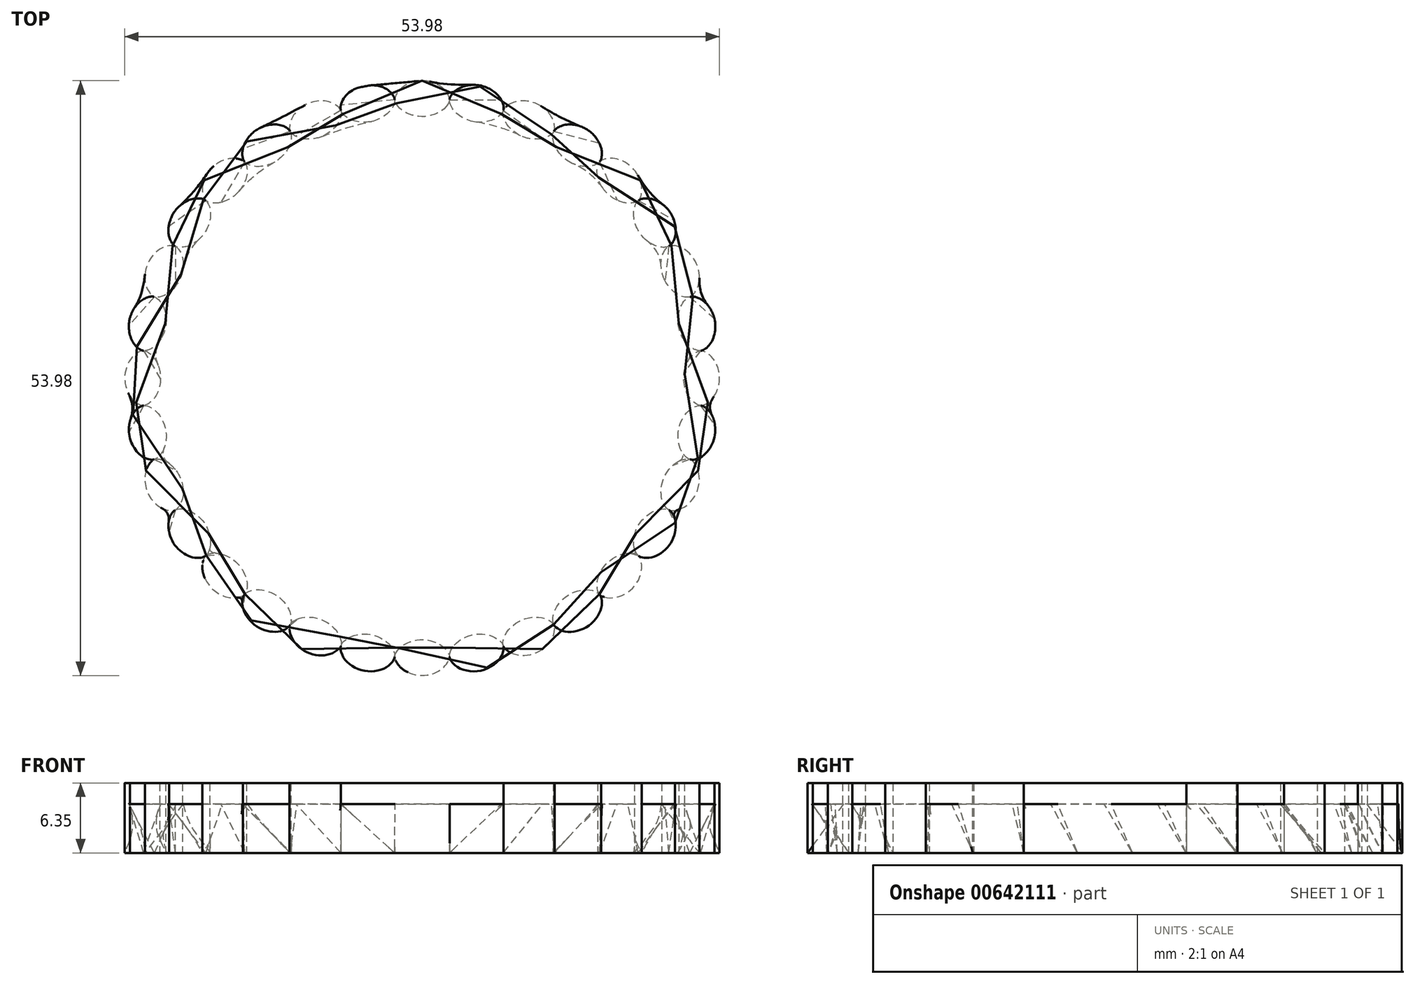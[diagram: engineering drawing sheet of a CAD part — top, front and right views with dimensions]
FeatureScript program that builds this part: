
annotation { "Feature Type Name" : "Feature", "Feature Type Description" : "" }
export const myFeature = defineFeature(function(context is Context, id is Id, definition is map)
    precondition{}
    {
        {
            var Q0;
            Q0=qCreatedBy(makeId("Top.planeOp"),FACE);
            var sketch = newSketch(context, id + "F0", { "sketchPlane" : qUnion([Q0])});
            skCircle(sketch, "E0", {"center": v(0, 0) * mm, "radius": 25.4 * mm, "construction": true});
            skCircle(sketch, "E1", {"center": v(0, 26.2) * mm, "radius": 0.8 * mm, "construction": true});
            skLineSegment(sketch, "E2", {"start": v(0, 26.99) * mm, "end": v(0, 26.2) * mm, "construction": true});
            skLineSegment(sketch, "E3", {"start": v(0, 0) * mm, "end": v(-4.8, 24.13) * mm, "construction": true});
            skCircle(sketch, "E4", {"center": v(-4.8, 24.13) * mm, "radius": 0.8 * mm, "construction": true});
            skLineSegment(sketch, "E5", {"start": v(0, 0) * mm, "end": v(0, 26.99) * mm, "construction": true});
            skCircle(sketch, "E6", {"center": v(0, 0) * mm, "radius": 26.99 * mm, "construction": true});
            skLineSegment(sketch, "E7", {"start": v(0, 0) * mm, "end": v(-2.49, 25.28) * mm, "construction": true});
            skLineSegment(sketch, "E8", {"start": v(0, 0) * mm, "end": v(-10.33, 24.93) * mm, "construction": true});
            skLineSegment(sketch, "E9", {"start": v(0, 0) * mm, "end": v(-7.37, 24.3) * mm, "construction": true});
            skCircle(sketch, "E10", {"center": v(-10.02, 24.2) * mm, "radius": 0.8 * mm, "construction": true});
            skCircle(sketch, "E11", {"center": v(-1.29, 26.16) * mm, "radius": 0.8 * mm, "construction": true});
            skCircle(sketch, "E12", {"center": v(-3.61, 24.34) * mm, "radius": 0.8 * mm, "construction": true});
            skLineSegment(sketch, "E13", {"start": v(-1.29, 26.16) * mm, "end": v(0, 0) * mm, "construction": true});
            skLineSegment(sketch, "E14", {"start": v(0, 0) * mm, "end": v(-3.61, 24.34) * mm, "construction": true});
            skLineSegment(sketch, "E15", {"start": v(-3.61, 24.34) * mm, "end": v(-2.83, 24.46) * mm, "construction": true});
            skLineSegment(sketch, "E16", {"start": v(-1.29, 26.16) * mm, "end": v(-2.08, 26.12) * mm, "construction": true});
            skPoint(sketch, "E17", {"position": v(-4.65, 23.35) * mm});
            skCircle(sketch, "E18", {"center": v(-5.98, 23.87) * mm, "radius": 0.8 * mm, "construction": true});
            skCircle(sketch, "E19", {"center": v(-8.82, 24.66) * mm, "radius": 0.8 * mm, "construction": true});
            skLineSegment(sketch, "E20", {"start": v(0, 0) * mm, "end": v(-5.98, 23.87) * mm, "construction": true});
            skLineSegment(sketch, "E21", {"start": v(0, 0) * mm, "end": v(-8.82, 24.66) * mm, "construction": true});
            skLineSegment(sketch, "E22", {"start": v(-5.98, 23.87) * mm, "end": v(-6.75, 23.68) * mm, "construction": true});
            skLineSegment(sketch, "E23", {"start": v(-8.82, 24.66) * mm, "end": v(-8.08, 24.93) * mm, "construction": true});
            skCircle(sketch, "E24", {"center": v(-0.64, 26.19) * mm, "radius": 0.8 * mm, "construction": true});
            skLineSegment(sketch, "E25", {"start": v(-0.64, 26.19) * mm, "end": v(0, 0) * mm, "construction": true});
            skCircle(sketch, "E26", {"center": v(-1.93, 26.12) * mm, "radius": 0.8 * mm, "construction": true});
            skLineSegment(sketch, "E27", {"start": v(-1.93, 26.12) * mm, "end": v(0, 0) * mm, "construction": true});
            skLineSegment(sketch, "E28", {"start": v(-0.64, 26.19) * mm, "end": v(-1.22, 26.73) * mm, "construction": true});
            skLineSegment(sketch, "E29", {"start": v(-1.93, 26.12) * mm, "end": v(-2.45, 25.52) * mm, "construction": true});
            skCircle(sketch, "E30", {"center": v(-3.01, 24.42) * mm, "radius": 0.8 * mm, "construction": true});
            skCircle(sketch, "E31", {"center": v(-4.2, 24.24) * mm, "radius": 0.8 * mm, "construction": true});
            skLineSegment(sketch, "E32", {"start": v(-3.01, 24.42) * mm, "end": v(0, 0) * mm, "construction": true});
            skLineSegment(sketch, "E33", {"start": v(-3.01, 24.42) * mm, "end": v(-2.52, 25.05) * mm, "construction": true});
            skLineSegment(sketch, "E34", {"start": v(-4.2, 24.24) * mm, "end": v(0, 0) * mm, "construction": true});
            skLineSegment(sketch, "E35", {"start": v(-4.2, 24.24) * mm, "end": v(-3.56, 23.79) * mm, "construction": true});
            skCircle(sketch, "E36", {"center": v(-5.4, 24) * mm, "radius": 0.8 * mm, "construction": true});
            skLineSegment(sketch, "E37", {"start": v(-5.4, 24) * mm, "end": v(0, 0) * mm, "construction": true});
            skLineSegment(sketch, "E38", {"start": v(-5.4, 24) * mm, "end": v(-5.82, 23.34) * mm, "construction": true});
            skCircle(sketch, "E39", {"center": v(-6.56, 23.71) * mm, "radius": 0.8 * mm, "construction": true});
            skCircle(sketch, "E40", {"center": v(-8.22, 24.87) * mm, "radius": 0.8 * mm, "construction": true});
            skCircle(sketch, "E41", {"center": v(-9.43, 24.44) * mm, "radius": 0.8 * mm, "construction": true});
            skLineSegment(sketch, "E42", {"start": v(-6.56, 23.71) * mm, "end": v(0, 0) * mm, "construction": true});
            skLineSegment(sketch, "E43", {"start": v(-6.56, 23.71) * mm, "end": v(-7.25, 24.1) * mm, "construction": true});
            skLineSegment(sketch, "E44", {"start": v(-8.22, 24.87) * mm, "end": v(0, 0) * mm, "construction": true});
            skLineSegment(sketch, "E45", {"start": v(-9.43, 24.44) * mm, "end": v(0, 0) * mm, "construction": true});
            skLineSegment(sketch, "E46", {"start": v(-8.22, 24.87) * mm, "end": v(-7.5, 24.51) * mm, "construction": true});
            skLineSegment(sketch, "E47", {"start": v(-9.43, 24.44) * mm, "end": v(-9.1, 25.16) * mm, "construction": true});
            skSolve(sketch);
        }
        {
            var Q0;
            Q0=qCreatedBy(makeId("Top.planeOp"),FACE);
            var sketch = newSketch(context, id + "F1", { "sketchPlane" : qUnion([Q0])});
            skPoint(sketch, "E48.0", {"position": v(0, 26.99) * mm});
            skPoint(sketch, "E48.1", {"position": v(-1.22, 26.73) * mm});
            skPoint(sketch, "E48.2", {"position": v(-2.08, 26.12) * mm});
            skPoint(sketch, "E48.3", {"position": v(-2.45, 25.52) * mm});
            skPoint(sketch, "E48.4", {"position": v(-2.49, 25.28) * mm});
            skPoint(sketch, "E48.5", {"position": v(-2.52, 25.05) * mm});
            skPoint(sketch, "E48.6", {"position": v(-2.83, 24.46) * mm});
            skPoint(sketch, "E48.7", {"position": v(-3.56, 23.79) * mm});
            skPoint(sketch, "E48.8", {"position": v(-4.65, 23.35) * mm});
            skPoint(sketch, "E48.9", {"position": v(-5.82, 23.34) * mm});
            skPoint(sketch, "E48.10", {"position": v(-6.75, 23.68) * mm});
            skPoint(sketch, "E48.11", {"position": v(-7.25, 24.1) * mm});
            skPoint(sketch, "E48.12", {"position": v(-7.37, 24.3) * mm});
            skPoint(sketch, "E48.13", {"position": v(-7.5, 24.51) * mm});
            skPoint(sketch, "E48.14", {"position": v(-8.08, 24.93) * mm});
            skPoint(sketch, "E48.15", {"position": v(-9.1, 25.16) * mm});
            skPoint(sketch, "E48.16", {"position": v(-10.33, 24.93) * mm});
            skLineSegment(sketch, "E49.0", {"start": v(0, 0) * mm, "end": v(0, 26.99) * mm, "construction": true});
            skLineSegment(sketch, "E49.1", {"start": v(0, 0) * mm, "end": v(-4.8, 24.13) * mm, "construction": true});
            skLineSegment(sketch, "E50.0", {"start": v(0, 0) * mm, "end": v(-10.33, 24.93) * mm, "construction": true});
            skPoint(sketch, "E51.1.1", {"position": v(-11.36, 24.23) * mm});
            skPoint(sketch, "E51.1.2", {"position": v(-11.92, 23.34) * mm});
            skPoint(sketch, "E51.1.3", {"position": v(-12.03, 22.64) * mm});
            skPoint(sketch, "E51.1.4", {"position": v(-11.97, 22.4) * mm});
            skPoint(sketch, "E51.1.5", {"position": v(-11.92, 22.17) * mm});
            skPoint(sketch, "E51.1.6", {"position": v(-11.97, 21.51) * mm});
            skPoint(sketch, "E51.1.7", {"position": v(-12.39, 20.61) * mm});
            skPoint(sketch, "E51.1.8", {"position": v(-13.23, 19.8) * mm});
            skPoint(sketch, "E51.1.9", {"position": v(-14.3, 19.34) * mm});
            skPoint(sketch, "E51.1.10", {"position": v(-15.3, 19.3) * mm});
            skPoint(sketch, "E51.1.11", {"position": v(-15.93, 19.5) * mm});
            skPoint(sketch, "E51.1.12", {"position": v(-16.11, 19.63) * mm});
            skPoint(sketch, "E51.1.13", {"position": v(-16.32, 19.78) * mm});
            skPoint(sketch, "E51.1.14", {"position": v(-17, 19.94) * mm});
            skPoint(sketch, "E51.1.15", {"position": v(-18.04, 19.76) * mm});
            skPoint(sketch, "E51.2.0", {"position": v(-19.08, 19.08) * mm});
            skPoint(sketch, "E51.2.1", {"position": v(-19.76, 18.04) * mm});
            skPoint(sketch, "E51.2.2", {"position": v(-19.94, 17) * mm});
            skPoint(sketch, "E51.2.3", {"position": v(-19.78, 16.32) * mm});
            skPoint(sketch, "E51.2.4", {"position": v(-19.63, 16.11) * mm});
            skPoint(sketch, "E51.2.5", {"position": v(-19.5, 15.93) * mm});
            skPoint(sketch, "E51.2.6", {"position": v(-19.3, 15.3) * mm});
            skPoint(sketch, "E51.2.7", {"position": v(-19.34, 14.3) * mm});
            skPoint(sketch, "E51.2.8", {"position": v(-19.8, 13.23) * mm});
            skPoint(sketch, "E51.2.9", {"position": v(-20.61, 12.39) * mm});
            skPoint(sketch, "E51.2.10", {"position": v(-21.51, 11.97) * mm});
            skPoint(sketch, "E51.2.11", {"position": v(-22.17, 11.92) * mm});
            skPoint(sketch, "E51.2.12", {"position": v(-22.4, 11.97) * mm});
            skPoint(sketch, "E51.2.13", {"position": v(-22.64, 12.03) * mm});
            skPoint(sketch, "E51.2.14", {"position": v(-23.34, 11.92) * mm});
            skPoint(sketch, "E51.2.15", {"position": v(-24.23, 11.36) * mm});
            skPoint(sketch, "E51.3.0", {"position": v(-24.93, 10.33) * mm});
            skPoint(sketch, "E51.3.1", {"position": v(-25.16, 9.1) * mm});
            skPoint(sketch, "E51.3.2", {"position": v(-24.93, 8.08) * mm});
            skPoint(sketch, "E51.3.3", {"position": v(-24.51, 7.5) * mm});
            skPoint(sketch, "E51.3.4", {"position": v(-24.3, 7.37) * mm});
            skPoint(sketch, "E51.3.5", {"position": v(-24.1, 7.25) * mm});
            skPoint(sketch, "E51.3.6", {"position": v(-23.68, 6.75) * mm});
            skPoint(sketch, "E51.3.7", {"position": v(-23.34, 5.82) * mm});
            skPoint(sketch, "E51.3.8", {"position": v(-23.35, 4.65) * mm});
            skPoint(sketch, "E51.3.9", {"position": v(-23.79, 3.56) * mm});
            skPoint(sketch, "E51.3.10", {"position": v(-24.46, 2.83) * mm});
            skPoint(sketch, "E51.3.11", {"position": v(-25.05, 2.52) * mm});
            skPoint(sketch, "E51.3.12", {"position": v(-25.28, 2.49) * mm});
            skPoint(sketch, "E51.3.13", {"position": v(-25.52, 2.45) * mm});
            skPoint(sketch, "E51.3.14", {"position": v(-26.12, 2.08) * mm});
            skPoint(sketch, "E51.3.15", {"position": v(-26.73, 1.22) * mm});
            skPoint(sketch, "E51.4.0", {"position": v(-26.99, 0) * mm});
            skPoint(sketch, "E51.4.1", {"position": v(-26.73, -1.22) * mm});
            skPoint(sketch, "E51.4.2", {"position": v(-26.12, -2.08) * mm});
            skPoint(sketch, "E51.4.3", {"position": v(-25.52, -2.45) * mm});
            skPoint(sketch, "E51.4.4", {"position": v(-25.28, -2.49) * mm});
            skPoint(sketch, "E51.4.5", {"position": v(-25.05, -2.52) * mm});
            skPoint(sketch, "E51.4.6", {"position": v(-24.46, -2.83) * mm});
            skPoint(sketch, "E51.4.7", {"position": v(-23.79, -3.56) * mm});
            skPoint(sketch, "E51.4.8", {"position": v(-23.35, -4.65) * mm});
            skPoint(sketch, "E51.4.9", {"position": v(-23.34, -5.82) * mm});
            skPoint(sketch, "E51.4.10", {"position": v(-23.68, -6.75) * mm});
            skPoint(sketch, "E51.4.11", {"position": v(-24.1, -7.25) * mm});
            skPoint(sketch, "E51.4.12", {"position": v(-24.3, -7.37) * mm});
            skPoint(sketch, "E51.4.13", {"position": v(-24.51, -7.5) * mm});
            skPoint(sketch, "E51.4.14", {"position": v(-24.93, -8.08) * mm});
            skPoint(sketch, "E51.4.15", {"position": v(-25.16, -9.1) * mm});
            skPoint(sketch, "E51.center", {"position": v(0, 0) * mm});
            skArc(sketch, "E52", {"start": v(3.5, -2.37) * mm, "mid": v(0, 4.23) * mm, "end": v(-3.5, -2.37) * mm});
            skLineSegment(sketch, "E53", {"start": v(-3.5, -2.37) * mm, "end": v(3.5, -2.37) * mm});
            skLineSegment(sketch, "E54", {"start": v(0, 4.23) * mm, "end": v(4.77, 4.23) * mm, "construction": true});
            skPoint(sketch, "E55.0.5.0", {"position": v(-19.76, -18.04) * mm});
            skPoint(sketch, "E55.1.5.0", {"position": v(-24.23, -11.36) * mm});
            skPoint(sketch, "E55.2.5.0", {"position": v(-23.34, -11.92) * mm});
            skPoint(sketch, "E55.3.5.0", {"position": v(-22.64, -12.03) * mm});
            skPoint(sketch, "E55.4.5.0", {"position": v(-22.4, -11.97) * mm});
            skPoint(sketch, "E55.5.5.0", {"position": v(-22.17, -11.92) * mm});
            skPoint(sketch, "E55.6.5.0", {"position": v(-21.51, -11.97) * mm});
            skPoint(sketch, "E55.7.5.0", {"position": v(-20.61, -12.39) * mm});
            skPoint(sketch, "E55.8.5.0", {"position": v(-19.8, -13.23) * mm});
            skPoint(sketch, "E55.9.5.0", {"position": v(-19.34, -14.3) * mm});
            skPoint(sketch, "E55.10.5.0", {"position": v(-19.3, -15.3) * mm});
            skPoint(sketch, "E55.11.5.0", {"position": v(-19.5, -15.93) * mm});
            skPoint(sketch, "E55.12.5.0", {"position": v(-19.63, -16.11) * mm});
            skPoint(sketch, "E55.13.5.0", {"position": v(-19.78, -16.32) * mm});
            skPoint(sketch, "E55.14.5.0", {"position": v(-19.94, -17) * mm});
            skPoint(sketch, "E55.15.5.0", {"position": v(-24.93, -10.33) * mm});
            skPoint(sketch, "E55.0.6.0", {"position": v(-11.36, -24.23) * mm});
            skPoint(sketch, "E55.1.6.0", {"position": v(-18.04, -19.76) * mm});
            skPoint(sketch, "E55.2.6.0", {"position": v(-17, -19.94) * mm});
            skPoint(sketch, "E55.3.6.0", {"position": v(-16.32, -19.78) * mm});
            skPoint(sketch, "E55.4.6.0", {"position": v(-16.11, -19.63) * mm});
            skPoint(sketch, "E55.5.6.0", {"position": v(-15.93, -19.5) * mm});
            skPoint(sketch, "E55.6.6.0", {"position": v(-15.3, -19.3) * mm});
            skPoint(sketch, "E55.7.6.0", {"position": v(-14.3, -19.34) * mm});
            skPoint(sketch, "E55.8.6.0", {"position": v(-13.23, -19.8) * mm});
            skPoint(sketch, "E55.9.6.0", {"position": v(-12.39, -20.61) * mm});
            skPoint(sketch, "E55.10.6.0", {"position": v(-11.97, -21.51) * mm});
            skPoint(sketch, "E55.11.6.0", {"position": v(-11.92, -22.17) * mm});
            skPoint(sketch, "E55.12.6.0", {"position": v(-11.97, -22.4) * mm});
            skPoint(sketch, "E55.13.6.0", {"position": v(-12.03, -22.64) * mm});
            skPoint(sketch, "E55.14.6.0", {"position": v(-11.92, -23.34) * mm});
            skPoint(sketch, "E55.15.6.0", {"position": v(-19.08, -19.08) * mm});
            skPoint(sketch, "E55.0.7.0", {"position": v(-1.22, -26.73) * mm});
            skPoint(sketch, "E55.1.7.0", {"position": v(-9.1, -25.16) * mm});
            skPoint(sketch, "E55.2.7.0", {"position": v(-8.08, -24.93) * mm});
            skPoint(sketch, "E55.3.7.0", {"position": v(-7.5, -24.51) * mm});
            skPoint(sketch, "E55.4.7.0", {"position": v(-7.37, -24.3) * mm});
            skPoint(sketch, "E55.5.7.0", {"position": v(-7.25, -24.1) * mm});
            skPoint(sketch, "E55.6.7.0", {"position": v(-6.75, -23.68) * mm});
            skPoint(sketch, "E55.7.7.0", {"position": v(-5.82, -23.34) * mm});
            skPoint(sketch, "E55.8.7.0", {"position": v(-4.65, -23.35) * mm});
            skPoint(sketch, "E55.9.7.0", {"position": v(-3.56, -23.79) * mm});
            skPoint(sketch, "E55.10.7.0", {"position": v(-2.83, -24.46) * mm});
            skPoint(sketch, "E55.11.7.0", {"position": v(-2.52, -25.05) * mm});
            skPoint(sketch, "E55.12.7.0", {"position": v(-2.49, -25.28) * mm});
            skPoint(sketch, "E55.13.7.0", {"position": v(-2.45, -25.52) * mm});
            skPoint(sketch, "E55.14.7.0", {"position": v(-2.08, -26.12) * mm});
            skPoint(sketch, "E55.15.7.0", {"position": v(-10.33, -24.93) * mm});
            skPoint(sketch, "E55.0.8.0", {"position": v(9.1, -25.16) * mm});
            skPoint(sketch, "E55.1.8.0", {"position": v(1.22, -26.73) * mm});
            skPoint(sketch, "E55.2.8.0", {"position": v(2.08, -26.12) * mm});
            skPoint(sketch, "E55.3.8.0", {"position": v(2.45, -25.52) * mm});
            skPoint(sketch, "E55.4.8.0", {"position": v(2.49, -25.28) * mm});
            skPoint(sketch, "E55.5.8.0", {"position": v(2.52, -25.05) * mm});
            skPoint(sketch, "E55.6.8.0", {"position": v(2.83, -24.46) * mm});
            skPoint(sketch, "E55.7.8.0", {"position": v(3.56, -23.79) * mm});
            skPoint(sketch, "E55.8.8.0", {"position": v(4.65, -23.35) * mm});
            skPoint(sketch, "E55.9.8.0", {"position": v(5.82, -23.34) * mm});
            skPoint(sketch, "E55.10.8.0", {"position": v(6.75, -23.68) * mm});
            skPoint(sketch, "E55.11.8.0", {"position": v(7.25, -24.1) * mm});
            skPoint(sketch, "E55.12.8.0", {"position": v(7.37, -24.3) * mm});
            skPoint(sketch, "E55.13.8.0", {"position": v(7.5, -24.51) * mm});
            skPoint(sketch, "E55.14.8.0", {"position": v(8.08, -24.93) * mm});
            skPoint(sketch, "E55.15.8.0", {"position": v(0, -26.99) * mm});
            skPoint(sketch, "E55.0.9.0", {"position": v(18.04, -19.76) * mm});
            skPoint(sketch, "E55.1.9.0", {"position": v(11.36, -24.23) * mm});
            skPoint(sketch, "E55.2.9.0", {"position": v(11.92, -23.34) * mm});
            skPoint(sketch, "E55.3.9.0", {"position": v(12.03, -22.64) * mm});
            skPoint(sketch, "E55.4.9.0", {"position": v(11.97, -22.4) * mm});
            skPoint(sketch, "E55.5.9.0", {"position": v(11.92, -22.17) * mm});
            skPoint(sketch, "E55.6.9.0", {"position": v(11.97, -21.51) * mm});
            skPoint(sketch, "E55.7.9.0", {"position": v(12.39, -20.61) * mm});
            skPoint(sketch, "E55.8.9.0", {"position": v(13.23, -19.8) * mm});
            skPoint(sketch, "E55.9.9.0", {"position": v(14.3, -19.34) * mm});
            skPoint(sketch, "E55.10.9.0", {"position": v(15.3, -19.3) * mm});
            skPoint(sketch, "E55.11.9.0", {"position": v(15.93, -19.5) * mm});
            skPoint(sketch, "E55.12.9.0", {"position": v(16.11, -19.63) * mm});
            skPoint(sketch, "E55.13.9.0", {"position": v(16.32, -19.78) * mm});
            skPoint(sketch, "E55.14.9.0", {"position": v(17, -19.94) * mm});
            skPoint(sketch, "E55.15.9.0", {"position": v(10.33, -24.93) * mm});
            skPoint(sketch, "E55.0.10.0", {"position": v(24.23, -11.36) * mm});
            skPoint(sketch, "E55.1.10.0", {"position": v(19.76, -18.04) * mm});
            skPoint(sketch, "E55.2.10.0", {"position": v(19.94, -17) * mm});
            skPoint(sketch, "E55.3.10.0", {"position": v(19.78, -16.32) * mm});
            skPoint(sketch, "E55.4.10.0", {"position": v(19.63, -16.11) * mm});
            skPoint(sketch, "E55.5.10.0", {"position": v(19.5, -15.93) * mm});
            skPoint(sketch, "E55.6.10.0", {"position": v(19.3, -15.3) * mm});
            skPoint(sketch, "E55.7.10.0", {"position": v(19.34, -14.3) * mm});
            skPoint(sketch, "E55.8.10.0", {"position": v(19.8, -13.23) * mm});
            skPoint(sketch, "E55.9.10.0", {"position": v(20.61, -12.39) * mm});
            skPoint(sketch, "E55.10.10.0", {"position": v(21.51, -11.97) * mm});
            skPoint(sketch, "E55.11.10.0", {"position": v(22.17, -11.92) * mm});
            skPoint(sketch, "E55.12.10.0", {"position": v(22.4, -11.97) * mm});
            skPoint(sketch, "E55.13.10.0", {"position": v(22.64, -12.03) * mm});
            skPoint(sketch, "E55.14.10.0", {"position": v(23.34, -11.92) * mm});
            skPoint(sketch, "E55.15.10.0", {"position": v(19.08, -19.08) * mm});
            skPoint(sketch, "E55.0.11.0", {"position": v(26.73, -1.22) * mm});
            skPoint(sketch, "E55.1.11.0", {"position": v(25.16, -9.1) * mm});
            skPoint(sketch, "E55.2.11.0", {"position": v(24.93, -8.08) * mm});
            skPoint(sketch, "E55.3.11.0", {"position": v(24.51, -7.5) * mm});
            skPoint(sketch, "E55.4.11.0", {"position": v(24.3, -7.37) * mm});
            skPoint(sketch, "E55.5.11.0", {"position": v(24.1, -7.25) * mm});
            skPoint(sketch, "E55.6.11.0", {"position": v(23.68, -6.75) * mm});
            skPoint(sketch, "E55.7.11.0", {"position": v(23.34, -5.82) * mm});
            skPoint(sketch, "E55.8.11.0", {"position": v(23.35, -4.65) * mm});
            skPoint(sketch, "E55.9.11.0", {"position": v(23.79, -3.56) * mm});
            skPoint(sketch, "E55.10.11.0", {"position": v(24.46, -2.83) * mm});
            skPoint(sketch, "E55.11.11.0", {"position": v(25.05, -2.52) * mm});
            skPoint(sketch, "E55.12.11.0", {"position": v(25.28, -2.49) * mm});
            skPoint(sketch, "E55.13.11.0", {"position": v(25.52, -2.45) * mm});
            skPoint(sketch, "E55.14.11.0", {"position": v(26.12, -2.08) * mm});
            skPoint(sketch, "E55.15.11.0", {"position": v(24.93, -10.33) * mm});
            skPoint(sketch, "E55.0.12.0", {"position": v(25.16, 9.1) * mm});
            skPoint(sketch, "E55.1.12.0", {"position": v(26.73, 1.22) * mm});
            skPoint(sketch, "E55.2.12.0", {"position": v(26.12, 2.08) * mm});
            skPoint(sketch, "E55.3.12.0", {"position": v(25.52, 2.45) * mm});
            skPoint(sketch, "E55.4.12.0", {"position": v(25.28, 2.49) * mm});
            skPoint(sketch, "E55.5.12.0", {"position": v(25.05, 2.52) * mm});
            skPoint(sketch, "E55.6.12.0", {"position": v(24.46, 2.83) * mm});
            skPoint(sketch, "E55.7.12.0", {"position": v(23.79, 3.56) * mm});
            skPoint(sketch, "E55.8.12.0", {"position": v(23.35, 4.65) * mm});
            skPoint(sketch, "E55.9.12.0", {"position": v(23.34, 5.82) * mm});
            skPoint(sketch, "E55.10.12.0", {"position": v(23.68, 6.75) * mm});
            skPoint(sketch, "E55.11.12.0", {"position": v(24.1, 7.25) * mm});
            skPoint(sketch, "E55.12.12.0", {"position": v(24.3, 7.37) * mm});
            skPoint(sketch, "E55.13.12.0", {"position": v(24.51, 7.5) * mm});
            skPoint(sketch, "E55.14.12.0", {"position": v(24.93, 8.08) * mm});
            skPoint(sketch, "E55.15.12.0", {"position": v(26.99, 0) * mm});
            skPoint(sketch, "E55.0.13.0", {"position": v(19.76, 18.04) * mm});
            skPoint(sketch, "E55.1.13.0", {"position": v(24.23, 11.36) * mm});
            skPoint(sketch, "E55.2.13.0", {"position": v(23.34, 11.92) * mm});
            skPoint(sketch, "E55.3.13.0", {"position": v(22.64, 12.03) * mm});
            skPoint(sketch, "E55.4.13.0", {"position": v(22.4, 11.97) * mm});
            skPoint(sketch, "E55.5.13.0", {"position": v(22.17, 11.92) * mm});
            skPoint(sketch, "E55.6.13.0", {"position": v(21.51, 11.97) * mm});
            skPoint(sketch, "E55.7.13.0", {"position": v(20.61, 12.39) * mm});
            skPoint(sketch, "E55.8.13.0", {"position": v(19.8, 13.23) * mm});
            skPoint(sketch, "E55.9.13.0", {"position": v(19.34, 14.3) * mm});
            skPoint(sketch, "E55.10.13.0", {"position": v(19.3, 15.3) * mm});
            skPoint(sketch, "E55.11.13.0", {"position": v(19.5, 15.93) * mm});
            skPoint(sketch, "E55.12.13.0", {"position": v(19.63, 16.11) * mm});
            skPoint(sketch, "E55.13.13.0", {"position": v(19.78, 16.32) * mm});
            skPoint(sketch, "E55.14.13.0", {"position": v(19.94, 17) * mm});
            skPoint(sketch, "E55.15.13.0", {"position": v(24.93, 10.33) * mm});
            skPoint(sketch, "E55.0.14.0", {"position": v(11.36, 24.23) * mm});
            skPoint(sketch, "E55.1.14.0", {"position": v(18.04, 19.76) * mm});
            skPoint(sketch, "E55.2.14.0", {"position": v(17, 19.94) * mm});
            skPoint(sketch, "E55.3.14.0", {"position": v(16.32, 19.78) * mm});
            skPoint(sketch, "E55.4.14.0", {"position": v(16.11, 19.63) * mm});
            skPoint(sketch, "E55.5.14.0", {"position": v(15.93, 19.5) * mm});
            skPoint(sketch, "E55.6.14.0", {"position": v(15.3, 19.3) * mm});
            skPoint(sketch, "E55.7.14.0", {"position": v(14.3, 19.34) * mm});
            skPoint(sketch, "E55.8.14.0", {"position": v(13.23, 19.8) * mm});
            skPoint(sketch, "E55.9.14.0", {"position": v(12.39, 20.61) * mm});
            skPoint(sketch, "E55.10.14.0", {"position": v(11.97, 21.51) * mm});
            skPoint(sketch, "E55.11.14.0", {"position": v(11.92, 22.17) * mm});
            skPoint(sketch, "E55.12.14.0", {"position": v(11.97, 22.4) * mm});
            skPoint(sketch, "E55.13.14.0", {"position": v(12.03, 22.64) * mm});
            skPoint(sketch, "E55.14.14.0", {"position": v(11.92, 23.34) * mm});
            skPoint(sketch, "E55.15.14.0", {"position": v(19.08, 19.08) * mm});
            skPoint(sketch, "E55.0.15.0", {"position": v(1.22, 26.73) * mm});
            skPoint(sketch, "E55.1.15.0", {"position": v(9.1, 25.16) * mm});
            skPoint(sketch, "E55.2.15.0", {"position": v(8.08, 24.93) * mm});
            skPoint(sketch, "E55.3.15.0", {"position": v(7.5, 24.51) * mm});
            skPoint(sketch, "E55.4.15.0", {"position": v(7.37, 24.3) * mm});
            skPoint(sketch, "E55.5.15.0", {"position": v(7.25, 24.1) * mm});
            skPoint(sketch, "E55.6.15.0", {"position": v(6.75, 23.68) * mm});
            skPoint(sketch, "E55.7.15.0", {"position": v(5.82, 23.34) * mm});
            skPoint(sketch, "E55.8.15.0", {"position": v(4.65, 23.35) * mm});
            skPoint(sketch, "E55.9.15.0", {"position": v(3.56, 23.79) * mm});
            skPoint(sketch, "E55.10.15.0", {"position": v(2.83, 24.46) * mm});
            skPoint(sketch, "E55.11.15.0", {"position": v(2.52, 25.05) * mm});
            skPoint(sketch, "E55.12.15.0", {"position": v(2.49, 25.28) * mm});
            skPoint(sketch, "E55.13.15.0", {"position": v(2.45, 25.52) * mm});
            skPoint(sketch, "E55.14.15.0", {"position": v(2.08, 26.12) * mm});
            skPoint(sketch, "E55.15.15.0", {"position": v(10.33, 24.93) * mm});
            skFitSpline(sketch, "E56", {"points": [v(0, 26.99) * mm, v(-1.22, 26.73) * mm, v(-2.08, 26.12) * mm, v(-2.45, 25.52) * mm, v(-2.49, 25.28) * mm, v(-2.52, 25.05) * mm, v(-2.83, 24.46) * mm, v(-3.56, 23.79) * mm, v(-4.65, 23.35) * mm, v(-5.82, 23.34) * mm, v(-6.75, 23.68) * mm, v(-7.25, 24.1) * mm, v(-7.37, 24.3) * mm, v(-7.5, 24.51) * mm, v(-8.08, 24.93) * mm, v(-9.1, 25.16) * mm, v(-10.33, 24.93) * mm, v(-11.36, 24.23) * mm, v(-11.92, 23.34) * mm, v(-12.03, 22.64) * mm, v(-11.97, 22.4) * mm, v(-11.92, 22.17) * mm, v(-11.97, 21.51) * mm, v(-12.39, 20.61) * mm, v(-13.23, 19.8) * mm, v(-14.3, 19.34) * mm, v(-15.3, 19.3) * mm, v(-15.93, 19.5) * mm, v(-16.11, 19.63) * mm, v(-16.32, 19.78) * mm, v(-17, 19.94) * mm, v(-18.04, 19.76) * mm, v(-19.08, 19.08) * mm, v(-19.76, 18.04) * mm, v(-19.94, 17) * mm, v(-19.78, 16.32) * mm, v(-19.63, 16.11) * mm, v(-19.5, 15.93) * mm, v(-19.3, 15.3) * mm, v(-19.34, 14.3) * mm, v(-19.8, 13.23) * mm, v(-20.61, 12.39) * mm, v(-21.51, 11.97) * mm, v(-22.17, 11.92) * mm, v(-22.4, 11.97) * mm, v(-22.64, 12.03) * mm, v(-23.34, 11.92) * mm, v(-24.23, 11.36) * mm, v(-24.93, 10.33) * mm, v(-25.16, 9.1) * mm, v(-24.93, 8.08) * mm, v(-24.51, 7.5) * mm, v(-24.3, 7.37) * mm, v(-24.1, 7.25) * mm, v(-23.68, 6.75) * mm, v(-23.34, 5.82) * mm, v(-23.35, 4.65) * mm, v(-23.79, 3.56) * mm, v(-24.46, 2.83) * mm, v(-25.05, 2.52) * mm, v(-25.28, 2.49) * mm, v(-25.52, 2.45) * mm, v(-26.12, 2.08) * mm, v(-26.73, 1.22) * mm, v(-26.99, 0) * mm, v(-26.73, -1.22) * mm, v(-26.12, -2.08) * mm, v(-25.52, -2.45) * mm, v(-25.28, -2.49) * mm, v(-25.05, -2.52) * mm, v(-24.46, -2.83) * mm, v(-23.79, -3.56) * mm, v(-23.35, -4.65) * mm, v(-23.34, -5.82) * mm, v(-23.68, -6.75) * mm, v(-24.1, -7.25) * mm, v(-24.3, -7.37) * mm, v(-24.51, -7.5) * mm, v(-24.93, -8.08) * mm, v(-25.16, -9.1) * mm, v(-24.93, -10.33) * mm, v(-24.23, -11.36) * mm, v(-23.34, -11.92) * mm, v(-22.64, -12.03) * mm, v(-22.4, -11.97) * mm, v(-22.17, -11.92) * mm, v(-21.51, -11.97) * mm, v(-20.61, -12.39) * mm, v(-19.8, -13.23) * mm, v(-19.34, -14.3) * mm, v(-19.3, -15.3) * mm, v(-19.5, -15.93) * mm, v(-19.63, -16.11) * mm, v(-19.78, -16.32) * mm, v(-19.94, -17) * mm, v(-19.76, -18.04) * mm, v(-19.08, -19.08) * mm, v(-18.04, -19.76) * mm, v(-17, -19.94) * mm, v(-16.32, -19.78) * mm, v(-16.11, -19.63) * mm, v(-15.93, -19.5) * mm, v(-15.3, -19.3) * mm, v(-14.3, -19.34) * mm, v(-13.23, -19.8) * mm, v(-12.39, -20.61) * mm, v(-11.97, -21.51) * mm, v(-11.92, -22.17) * mm, v(-11.97, -22.4) * mm, v(-12.03, -22.64) * mm, v(-11.92, -23.34) * mm, v(-11.36, -24.23) * mm, v(-10.33, -24.93) * mm, v(-9.1, -25.16) * mm, v(-8.08, -24.93) * mm, v(-7.5, -24.51) * mm, v(-7.37, -24.3) * mm, v(-7.25, -24.1) * mm, v(-6.75, -23.68) * mm, v(-5.82, -23.34) * mm, v(-4.65, -23.35) * mm, v(-3.56, -23.79) * mm, v(-2.83, -24.46) * mm, v(-2.52, -25.05) * mm, v(-2.49, -25.28) * mm, v(-2.45, -25.52) * mm, v(-2.08, -26.12) * mm, v(-1.22, -26.73) * mm, v(0, -26.99) * mm, v(1.22, -26.73) * mm, v(2.08, -26.12) * mm, v(2.45, -25.52) * mm, v(2.49, -25.28) * mm, v(2.52, -25.05) * mm, v(2.83, -24.46) * mm, v(3.56, -23.79) * mm, v(4.65, -23.35) * mm, v(5.82, -23.34) * mm, v(6.75, -23.68) * mm, v(7.25, -24.1) * mm, v(7.37, -24.3) * mm, v(7.5, -24.51) * mm, v(8.08, -24.93) * mm, v(9.1, -25.16) * mm, v(10.33, -24.93) * mm, v(11.36, -24.23) * mm, v(11.92, -23.34) * mm, v(12.03, -22.64) * mm, v(11.97, -22.4) * mm, v(11.92, -22.17) * mm, v(11.97, -21.51) * mm, v(12.39, -20.61) * mm, v(13.23, -19.8) * mm, v(14.3, -19.34) * mm, v(15.3, -19.3) * mm, v(15.93, -19.5) * mm, v(16.11, -19.63) * mm, v(16.32, -19.78) * mm, v(17, -19.94) * mm, v(18.04, -19.76) * mm, v(19.08, -19.08) * mm, v(19.76, -18.04) * mm, v(19.94, -17) * mm, v(19.78, -16.32) * mm, v(19.63, -16.11) * mm, v(19.5, -15.93) * mm, v(19.3, -15.3) * mm, v(19.34, -14.3) * mm, v(19.8, -13.23) * mm, v(20.61, -12.39) * mm, v(21.51, -11.97) * mm, v(22.17, -11.92) * mm, v(22.4, -11.97) * mm, v(22.64, -12.03) * mm, v(23.34, -11.92) * mm, v(24.23, -11.36) * mm, v(24.93, -10.33) * mm, v(25.16, -9.1) * mm, v(24.93, -8.08) * mm, v(24.51, -7.5) * mm, v(24.3, -7.37) * mm, v(24.1, -7.25) * mm, v(23.68, -6.75) * mm, v(23.34, -5.82) * mm, v(23.35, -4.65) * mm, v(23.79, -3.56) * mm, v(24.46, -2.83) * mm, v(25.05, -2.52) * mm, v(25.28, -2.49) * mm, v(25.52, -2.45) * mm, v(26.12, -2.08) * mm, v(26.73, -1.22) * mm, v(26.99, 0) * mm, v(26.73, 1.22) * mm, v(26.12, 2.08) * mm, v(25.52, 2.45) * mm, v(25.28, 2.49) * mm, v(25.05, 2.52) * mm, v(24.46, 2.83) * mm, v(23.79, 3.56) * mm, v(23.35, 4.65) * mm, v(23.34, 5.82) * mm, v(23.68, 6.75) * mm, v(24.1, 7.25) * mm, v(24.3, 7.37) * mm, v(24.51, 7.5) * mm, v(24.93, 8.08) * mm, v(25.16, 9.1) * mm, v(24.93, 10.33) * mm, v(24.23, 11.36) * mm, v(23.34, 11.92) * mm, v(22.64, 12.03) * mm, v(22.4, 11.97) * mm, v(22.17, 11.92) * mm, v(21.51, 11.97) * mm, v(20.61, 12.39) * mm, v(19.8, 13.23) * mm, v(19.34, 14.3) * mm, v(19.3, 15.3) * mm, v(19.5, 15.93) * mm, v(19.63, 16.11) * mm, v(19.78, 16.32) * mm, v(19.94, 17) * mm, v(19.76, 18.04) * mm, v(19.08, 19.08) * mm, v(18.04, 19.76) * mm, v(17, 19.94) * mm, v(16.32, 19.78) * mm, v(16.11, 19.63) * mm, v(15.93, 19.5) * mm, v(15.3, 19.3) * mm, v(14.3, 19.34) * mm, v(13.23, 19.8) * mm, v(12.39, 20.61) * mm, v(11.97, 21.51) * mm, v(11.92, 22.17) * mm, v(11.97, 22.4) * mm, v(12.03, 22.64) * mm, v(11.92, 23.34) * mm, v(11.36, 24.23) * mm, v(10.33, 24.93) * mm, v(9.1, 25.16) * mm, v(8.08, 24.93) * mm, v(7.5, 24.51) * mm, v(7.37, 24.3) * mm, v(7.25, 24.1) * mm, v(6.75, 23.68) * mm, v(5.82, 23.34) * mm, v(4.65, 23.35) * mm, v(3.56, 23.79) * mm, v(2.83, 24.46) * mm, v(2.52, 25.05) * mm, v(2.49, 25.28) * mm, v(2.45, 25.52) * mm, v(2.08, 26.12) * mm, v(1.22, 26.73) * mm, v(0, 26.99) * mm]});
            skSolve(sketch);
        }
        {
            var Q0;
            Q0=makeQuery(id+"F1.imprint","IMPRINT",FACE,{"disambiguationData":[TD([[makeQuery(id+"F1.imprint","IMPRINT",EDGE,{"derivedFrom":sQuery(id+"F1.wireOp",EDGE,"1fc19522-54e3-439c-a8f5-bc840eb4e19d")}),1.0]])]});
            var Q1;
            Q1=makeQuery(id+"F1.imprint","IMPRINT",FACE,{"disambiguationData":[TD([[makeQuery(id+"F1.imprint","IMPRINT",EDGE,{"derivedFrom":sQuery(id+"F1.wireOp",EDGE,"E52")}),-1.0]])]});
            var Q2;
            Q2=makeQuery(id+"F1.imprint","IMPRINT",FACE,{"disambiguationData":[TD([[makeQuery(id+"F1.imprint","IMPRINT",EDGE,{"derivedFrom":sQuery(id+"F1.wireOp",EDGE,"E52")}),1.0]])]});
            extrude(context, id + "F2", {"entities" : qUnion([Q0, Q1, Q2]), "depth" : 6.35 * mm, "offsetDistance" : 25.4 * mm});
        }
        {
            var Q0;
            Q0=makeQuery(id+"F2.opExtrude","CAP_FACE",FACE,{"disambiguationData":[OSD([sQuery(id+"F1.wireOp",EDGE,"E52"),sQuery(id+"F1.wireOp",EDGE,"E53"),sQuery(id+"F1.wireOp",EDGE,"E56")])],"isStart":true});
            var sketch = newSketch(context, id + "F3", { "sketchPlane" : qUnion([Q0])});
            skFitSpline(sketch, "E57.0", {"points": [v(0, -26.99) * mm, v(-0.42, -26.99) * mm, v(-1.24, -26.81) * mm, v(-2.1, -26.2) * mm, v(-2.47, -25.55) * mm, v(-2.5, -25.28) * mm, v(-2.5, -25.02) * mm, v(-2.8, -24.39) * mm, v(-3.53, -23.72) * mm, v(-4.63, -23.28) * mm, v(-5.81, -23.27) * mm, v(-6.74, -23.6) * mm, v(-7.26, -24.08) * mm, v(-7.37, -24.3) * mm, v(-7.5, -24.55) * mm, v(-8.09, -25.01) * mm, v(-9.12, -25.24) * mm, v(-10.36, -25.02) * mm, v(-11.4, -24.3) * mm, v(-11.97, -23.4) * mm, v(-12.06, -22.66) * mm, v(-11.97, -22.4) * mm, v(-11.89, -22.16) * mm, v(-11.92, -21.46) * mm, v(-12.34, -20.57) * mm, v(-13.19, -19.74) * mm, v(-14.28, -19.27) * mm, v(-15.26, -19.23) * mm, v(-15.92, -19.47) * mm, v(-16.11, -19.64) * mm, v(-16.32, -19.81) * mm, v(-17.04, -20.01) * mm, v(-18.08, -19.83) * mm, v(-19.15, -19.15) * mm, v(-19.83, -18.08) * mm, v(-20.01, -17.04) * mm, v(-19.81, -16.32) * mm, v(-19.64, -16.11) * mm, v(-19.47, -15.92) * mm, v(-19.23, -15.26) * mm, v(-19.27, -14.28) * mm, v(-19.74, -13.19) * mm, v(-20.57, -12.34) * mm, v(-21.46, -11.92) * mm, v(-22.16, -11.89) * mm, v(-22.4, -11.97) * mm, v(-22.66, -12.06) * mm, v(-23.4, -11.97) * mm, v(-24.3, -11.4) * mm, v(-25.02, -10.36) * mm, v(-25.24, -9.12) * mm, v(-25.01, -8.09) * mm, v(-24.55, -7.5) * mm, v(-24.3, -7.37) * mm, v(-24.08, -7.26) * mm, v(-23.6, -6.74) * mm, v(-23.27, -5.81) * mm, v(-23.28, -4.63) * mm, v(-23.72, -3.53) * mm, v(-24.39, -2.8) * mm, v(-25.02, -2.5) * mm, v(-25.28, -2.5) * mm, v(-25.55, -2.47) * mm, v(-26.2, -2.1) * mm, v(-26.81, -1.24) * mm, v(-27.08, 0) * mm, v(-26.81, 1.24) * mm, v(-26.2, 2.1) * mm, v(-25.55, 2.47) * mm, v(-25.28, 2.5) * mm, v(-25.02, 2.5) * mm, v(-24.39, 2.8) * mm, v(-23.72, 3.53) * mm, v(-23.28, 4.63) * mm, v(-23.27, 5.81) * mm, v(-23.6, 6.74) * mm, v(-24.08, 7.26) * mm, v(-24.3, 7.37) * mm, v(-24.55, 7.5) * mm, v(-25.01, 8.09) * mm, v(-25.24, 9.12) * mm, v(-25.02, 10.36) * mm, v(-24.3, 11.4) * mm, v(-23.4, 11.97) * mm, v(-22.66, 12.06) * mm, v(-22.4, 11.97) * mm, v(-22.16, 11.89) * mm, v(-21.46, 11.92) * mm, v(-20.57, 12.34) * mm, v(-19.74, 13.19) * mm, v(-19.27, 14.28) * mm, v(-19.23, 15.26) * mm, v(-19.47, 15.92) * mm, v(-19.64, 16.11) * mm, v(-19.81, 16.32) * mm, v(-20.01, 17.04) * mm, v(-19.83, 18.08) * mm, v(-19.15, 19.15) * mm, v(-18.08, 19.83) * mm, v(-17.04, 20.01) * mm, v(-16.32, 19.81) * mm, v(-16.11, 19.64) * mm, v(-15.92, 19.47) * mm, v(-15.26, 19.23) * mm, v(-14.28, 19.27) * mm, v(-13.19, 19.74) * mm, v(-12.34, 20.57) * mm, v(-11.92, 21.46) * mm, v(-11.89, 22.16) * mm, v(-11.97, 22.4) * mm, v(-12.06, 22.66) * mm, v(-11.97, 23.4) * mm, v(-11.4, 24.3) * mm, v(-10.36, 25.02) * mm, v(-9.12, 25.24) * mm, v(-8.09, 25.01) * mm, v(-7.5, 24.55) * mm, v(-7.37, 24.3) * mm, v(-7.26, 24.08) * mm, v(-6.74, 23.6) * mm, v(-5.81, 23.27) * mm, v(-4.63, 23.28) * mm, v(-3.53, 23.72) * mm, v(-2.8, 24.39) * mm, v(-2.5, 25.02) * mm, v(-2.5, 25.28) * mm, v(-2.47, 25.55) * mm, v(-2.1, 26.2) * mm, v(-1.24, 26.81) * mm, v(0, 27.08) * mm, v(1.24, 26.81) * mm, v(2.1, 26.2) * mm, v(2.47, 25.55) * mm, v(2.5, 25.28) * mm, v(2.5, 25.02) * mm, v(2.8, 24.39) * mm, v(3.53, 23.72) * mm, v(4.63, 23.28) * mm, v(5.81, 23.27) * mm, v(6.74, 23.6) * mm, v(7.26, 24.08) * mm, v(7.37, 24.3) * mm, v(7.5, 24.55) * mm, v(8.09, 25.01) * mm, v(9.12, 25.24) * mm, v(10.36, 25.02) * mm, v(11.4, 24.3) * mm, v(11.97, 23.4) * mm, v(12.06, 22.66) * mm, v(11.97, 22.4) * mm, v(11.89, 22.16) * mm, v(11.92, 21.46) * mm, v(12.34, 20.57) * mm, v(13.19, 19.74) * mm, v(14.28, 19.27) * mm, v(15.26, 19.23) * mm, v(15.92, 19.47) * mm, v(16.11, 19.64) * mm, v(16.32, 19.81) * mm, v(17.04, 20.01) * mm, v(18.08, 19.83) * mm, v(19.15, 19.15) * mm, v(19.83, 18.08) * mm, v(20.01, 17.04) * mm, v(19.81, 16.32) * mm, v(19.64, 16.11) * mm, v(19.47, 15.92) * mm, v(19.23, 15.26) * mm, v(19.27, 14.28) * mm, v(19.74, 13.19) * mm, v(20.57, 12.34) * mm, v(21.46, 11.92) * mm, v(22.16, 11.89) * mm, v(22.4, 11.97) * mm, v(22.66, 12.06) * mm, v(23.4, 11.97) * mm, v(24.3, 11.4) * mm, v(25.02, 10.36) * mm, v(25.24, 9.12) * mm, v(25.01, 8.09) * mm, v(24.55, 7.5) * mm, v(24.3, 7.37) * mm, v(24.08, 7.26) * mm, v(23.6, 6.74) * mm, v(23.27, 5.81) * mm, v(23.28, 4.63) * mm, v(23.72, 3.53) * mm, v(24.39, 2.8) * mm, v(25.02, 2.5) * mm, v(25.28, 2.5) * mm, v(25.55, 2.47) * mm, v(26.2, 2.1) * mm, v(26.81, 1.24) * mm, v(27.08, 0) * mm, v(26.81, -1.24) * mm, v(26.2, -2.1) * mm, v(25.55, -2.47) * mm, v(25.28, -2.5) * mm, v(25.02, -2.5) * mm, v(24.39, -2.8) * mm, v(23.72, -3.53) * mm, v(23.28, -4.63) * mm, v(23.27, -5.81) * mm, v(23.6, -6.74) * mm, v(24.08, -7.26) * mm, v(24.3, -7.37) * mm, v(24.55, -7.5) * mm, v(25.01, -8.09) * mm, v(25.24, -9.12) * mm, v(25.02, -10.36) * mm, v(24.3, -11.4) * mm, v(23.4, -11.97) * mm, v(22.66, -12.06) * mm, v(22.4, -11.97) * mm, v(22.16, -11.89) * mm, v(21.46, -11.92) * mm, v(20.57, -12.34) * mm, v(19.74, -13.19) * mm, v(19.27, -14.28) * mm, v(19.23, -15.26) * mm, v(19.47, -15.92) * mm, v(19.64, -16.11) * mm, v(19.81, -16.32) * mm, v(20.01, -17.04) * mm, v(19.83, -18.08) * mm, v(19.15, -19.15) * mm, v(18.08, -19.83) * mm, v(17.04, -20.01) * mm, v(16.32, -19.81) * mm, v(16.11, -19.64) * mm, v(15.92, -19.47) * mm, v(15.26, -19.23) * mm, v(14.28, -19.27) * mm, v(13.19, -19.74) * mm, v(12.34, -20.57) * mm, v(11.92, -21.46) * mm, v(11.89, -22.16) * mm, v(11.97, -22.4) * mm, v(12.06, -22.66) * mm, v(11.97, -23.4) * mm, v(11.4, -24.3) * mm, v(10.36, -25.02) * mm, v(9.12, -25.24) * mm, v(8.09, -25.01) * mm, v(7.5, -24.55) * mm, v(7.37, -24.3) * mm, v(7.26, -24.08) * mm, v(6.74, -23.6) * mm, v(5.81, -23.27) * mm, v(4.63, -23.28) * mm, v(3.53, -23.72) * mm, v(2.8, -24.39) * mm, v(2.5, -25.02) * mm, v(2.5, -25.28) * mm, v(2.47, -25.55) * mm, v(2.1, -26.2) * mm, v(1.24, -26.81) * mm, v(0.42, -26.99) * mm, v(0, -26.99) * mm]});
            skCircle(sketch, "E58", {"center": v(0, 0) * mm, "radius": 4.1 * mm, "construction": true});
            skSolve(sketch);
        }
        {
            var Q0;
            Q0=qCreatedBy(makeId("Top.planeOp"),FACE);
            cPlane(context, id + "F4", {"entities" : qUnion([Q0]), "cplaneType" : CPlaneType.OFFSET, "offset" : 4.44 * mm, "width" : 152.4 * mm, "height" : 152.4 * mm});
        }
        {
            var Q0;
            Q0=makeQuery(id+"F2.opExtrude","SWEPT_BODY",BODY,{"disambiguationData":[OSD([sQuery(id+"F1.wireOp",EDGE,"E52"),sQuery(id+"F1.wireOp",EDGE,"E53"),sQuery(id+"F1.wireOp",EDGE,"E56")])]});
            var Q1;
            Q1=sQuery(id+"F3.wireOp",EDGE,"E58");
            transform(context, id + "F5", {"entities" : qUnion([Q0]), "transformType" : TransformType.ROTATION, "transformAxis" : qUnion([Q1]), "angle" : (360 / (16 * 2)) * degree, "makeCopy" : true});
        }
        {
            var Q0;
            Q0=qCreatedBy(id+"F4.planeOp",FACE);
            var sketch = newSketch(context, id + "F6", { "sketchPlane" : qUnion([Q0])});
            skFitSpline(sketch, "E59.0", {"points": [v(-5.27, 26.47) * mm, v(-5.68, 26.39) * mm, v(-6.44, 26.05) * mm, v(-7.17, 25.29) * mm, v(-7.4, 24.58) * mm, v(-7.37, 24.3) * mm, v(-7.34, 24.06) * mm, v(-7.5, 23.37) * mm, v(-8.1, 22.58) * mm, v(-9.08, 21.93) * mm, v(-10.24, 21.69) * mm, v(-11.22, 21.84) * mm, v(-11.82, 22.2) * mm, v(-11.97, 22.4) * mm, v(-12.14, 22.61) * mm, v(-12.81, 22.95) * mm, v(-13.87, 22.98) * mm, v(-15.04, 22.52) * mm, v(-15.92, 21.6) * mm, v(-16.3, 20.62) * mm, v(-16.25, 19.87) * mm, v(-16.11, 19.63) * mm, v(-15.98, 19.42) * mm, v(-15.88, 18.72) * mm, v(-16.12, 17.76) * mm, v(-16.78, 16.78) * mm, v(-17.76, 16.12) * mm, v(-18.72, 15.88) * mm, v(-19.42, 15.98) * mm, v(-19.63, 16.11) * mm, v(-19.87, 16.25) * mm, v(-20.62, 16.3) * mm, v(-21.6, 15.92) * mm, v(-22.52, 15.04) * mm, v(-22.98, 13.87) * mm, v(-22.95, 12.81) * mm, v(-22.61, 12.14) * mm, v(-22.4, 11.97) * mm, v(-22.2, 11.82) * mm, v(-21.84, 11.22) * mm, v(-21.69, 10.24) * mm, v(-21.93, 9.08) * mm, v(-22.58, 8.1) * mm, v(-23.37, 7.5) * mm, v(-24.06, 7.34) * mm, v(-24.3, 7.37) * mm, v(-24.58, 7.4) * mm, v(-25.29, 7.17) * mm, v(-26.05, 6.44) * mm, v(-26.56, 5.28) * mm, v(-26.54, 4.02) * mm, v(-26.1, 3.05) * mm, v(-25.54, 2.56) * mm, v(-25.28, 2.49) * mm, v(-25.03, 2.43) * mm, v(-24.47, 2) * mm, v(-23.96, 1.16) * mm, v(-23.74, 0) * mm, v(-23.96, -1.16) * mm, v(-24.47, -2) * mm, v(-25.03, -2.43) * mm, v(-25.28, -2.49) * mm, v(-25.54, -2.56) * mm, v(-26.1, -3.05) * mm, v(-26.54, -4.02) * mm, v(-26.56, -5.28) * mm, v(-26.05, -6.44) * mm, v(-25.29, -7.17) * mm, v(-24.58, -7.4) * mm, v(-24.3, -7.37) * mm, v(-24.06, -7.34) * mm, v(-23.37, -7.5) * mm, v(-22.58, -8.1) * mm, v(-21.93, -9.08) * mm, v(-21.69, -10.24) * mm, v(-21.84, -11.22) * mm, v(-22.2, -11.82) * mm, v(-22.4, -11.97) * mm, v(-22.61, -12.14) * mm, v(-22.95, -12.81) * mm, v(-22.98, -13.87) * mm, v(-22.52, -15.04) * mm, v(-21.6, -15.92) * mm, v(-20.62, -16.3) * mm, v(-19.87, -16.25) * mm, v(-19.63, -16.11) * mm, v(-19.42, -15.98) * mm, v(-18.72, -15.88) * mm, v(-17.76, -16.12) * mm, v(-16.78, -16.78) * mm, v(-16.12, -17.76) * mm, v(-15.88, -18.72) * mm, v(-15.98, -19.42) * mm, v(-16.11, -19.63) * mm, v(-16.25, -19.87) * mm, v(-16.3, -20.62) * mm, v(-15.92, -21.6) * mm, v(-15.04, -22.52) * mm, v(-13.87, -22.98) * mm, v(-12.81, -22.95) * mm, v(-12.14, -22.61) * mm, v(-11.97, -22.4) * mm, v(-11.82, -22.2) * mm, v(-11.22, -21.84) * mm, v(-10.24, -21.69) * mm, v(-9.08, -21.93) * mm, v(-8.1, -22.58) * mm, v(-7.5, -23.37) * mm, v(-7.34, -24.06) * mm, v(-7.37, -24.3) * mm, v(-7.4, -24.58) * mm, v(-7.17, -25.29) * mm, v(-6.44, -26.05) * mm, v(-5.28, -26.56) * mm, v(-4.02, -26.54) * mm, v(-3.05, -26.1) * mm, v(-2.56, -25.54) * mm, v(-2.49, -25.28) * mm, v(-2.43, -25.03) * mm, v(-2, -24.47) * mm, v(-1.16, -23.96) * mm, v(0, -23.74) * mm, v(1.16, -23.96) * mm, v(2, -24.47) * mm, v(2.43, -25.03) * mm, v(2.49, -25.28) * mm, v(2.56, -25.54) * mm, v(3.05, -26.1) * mm, v(4.02, -26.54) * mm, v(5.28, -26.56) * mm, v(6.44, -26.05) * mm, v(7.17, -25.29) * mm, v(7.4, -24.58) * mm, v(7.37, -24.3) * mm, v(7.34, -24.06) * mm, v(7.5, -23.37) * mm, v(8.1, -22.58) * mm, v(9.08, -21.93) * mm, v(10.24, -21.69) * mm, v(11.22, -21.84) * mm, v(11.82, -22.2) * mm, v(11.97, -22.4) * mm, v(12.14, -22.61) * mm, v(12.81, -22.95) * mm, v(13.87, -22.98) * mm, v(15.04, -22.52) * mm, v(15.92, -21.6) * mm, v(16.3, -20.62) * mm, v(16.25, -19.87) * mm, v(16.11, -19.63) * mm, v(15.98, -19.42) * mm, v(15.88, -18.72) * mm, v(16.12, -17.76) * mm, v(16.78, -16.78) * mm, v(17.76, -16.12) * mm, v(18.72, -15.88) * mm, v(19.42, -15.98) * mm, v(19.63, -16.11) * mm, v(19.87, -16.25) * mm, v(20.62, -16.3) * mm, v(21.6, -15.92) * mm, v(22.52, -15.04) * mm, v(22.98, -13.87) * mm, v(22.95, -12.81) * mm, v(22.61, -12.14) * mm, v(22.4, -11.97) * mm, v(22.2, -11.82) * mm, v(21.84, -11.22) * mm, v(21.69, -10.24) * mm, v(21.93, -9.08) * mm, v(22.58, -8.1) * mm, v(23.37, -7.5) * mm, v(24.06, -7.34) * mm, v(24.3, -7.37) * mm, v(24.58, -7.4) * mm, v(25.29, -7.17) * mm, v(26.05, -6.44) * mm, v(26.56, -5.28) * mm, v(26.54, -4.02) * mm, v(26.1, -3.05) * mm, v(25.54, -2.56) * mm, v(25.28, -2.49) * mm, v(25.03, -2.43) * mm, v(24.47, -2) * mm, v(23.96, -1.16) * mm, v(23.74, 0) * mm, v(23.96, 1.16) * mm, v(24.47, 2) * mm, v(25.03, 2.43) * mm, v(25.28, 2.49) * mm, v(25.54, 2.56) * mm, v(26.1, 3.05) * mm, v(26.54, 4.02) * mm, v(26.56, 5.28) * mm, v(26.05, 6.44) * mm, v(25.29, 7.17) * mm, v(24.58, 7.4) * mm, v(24.3, 7.37) * mm, v(24.06, 7.34) * mm, v(23.37, 7.5) * mm, v(22.58, 8.1) * mm, v(21.93, 9.08) * mm, v(21.69, 10.24) * mm, v(21.84, 11.22) * mm, v(22.2, 11.82) * mm, v(22.4, 11.97) * mm, v(22.61, 12.14) * mm, v(22.95, 12.81) * mm, v(22.98, 13.87) * mm, v(22.52, 15.04) * mm, v(21.6, 15.92) * mm, v(20.62, 16.3) * mm, v(19.87, 16.25) * mm, v(19.63, 16.11) * mm, v(19.42, 15.98) * mm, v(18.72, 15.88) * mm, v(17.76, 16.12) * mm, v(16.78, 16.78) * mm, v(16.12, 17.76) * mm, v(15.88, 18.72) * mm, v(15.98, 19.42) * mm, v(16.11, 19.63) * mm, v(16.25, 19.87) * mm, v(16.3, 20.62) * mm, v(15.92, 21.6) * mm, v(15.04, 22.52) * mm, v(13.87, 22.98) * mm, v(12.81, 22.95) * mm, v(12.14, 22.61) * mm, v(11.97, 22.4) * mm, v(11.82, 22.2) * mm, v(11.22, 21.84) * mm, v(10.24, 21.69) * mm, v(9.08, 21.93) * mm, v(8.1, 22.58) * mm, v(7.5, 23.37) * mm, v(7.34, 24.06) * mm, v(7.37, 24.3) * mm, v(7.4, 24.58) * mm, v(7.17, 25.29) * mm, v(6.44, 26.05) * mm, v(5.28, 26.56) * mm, v(4.02, 26.54) * mm, v(3.05, 26.1) * mm, v(2.56, 25.54) * mm, v(2.49, 25.28) * mm, v(2.43, 25.03) * mm, v(2, 24.47) * mm, v(1.16, 23.96) * mm, v(0, 23.74) * mm, v(-1.16, 23.96) * mm, v(-2, 24.47) * mm, v(-2.43, 25.03) * mm, v(-2.49, 25.28) * mm, v(-2.56, 25.54) * mm, v(-3.05, 26.1) * mm, v(-4.02, 26.54) * mm, v(-4.85, 26.55) * mm, v(-5.27, 26.47) * mm]});
            skSolve(sketch);
        }
        {
            var Q0;
            Q0=makeQuery(id+"F3.imprint","IMPRINT",FACE,{"disambiguationData":[TD([[makeQuery(id+"F3.imprint","IMPRINT",EDGE,{"derivedFrom":sQuery(id+"F3.wireOp",EDGE,"E57.0")}),-1.0]])]});
            var Q1;
            Q1=makeQuery(id+"F6.imprint","IMPRINT",FACE,{"disambiguationData":[TD([[makeQuery(id+"F6.imprint","IMPRINT",EDGE,{"derivedFrom":sQuery(id+"F6.wireOp",EDGE,"E59.0")}),1.0]])]});
            loft(context, id + "F7", {"sheetProfilesArray" : [{ "sheetProfileEntities" : qUnion([Q0]) }, { "sheetProfileEntities" : qUnion([Q1]) }]});
        }
    });
